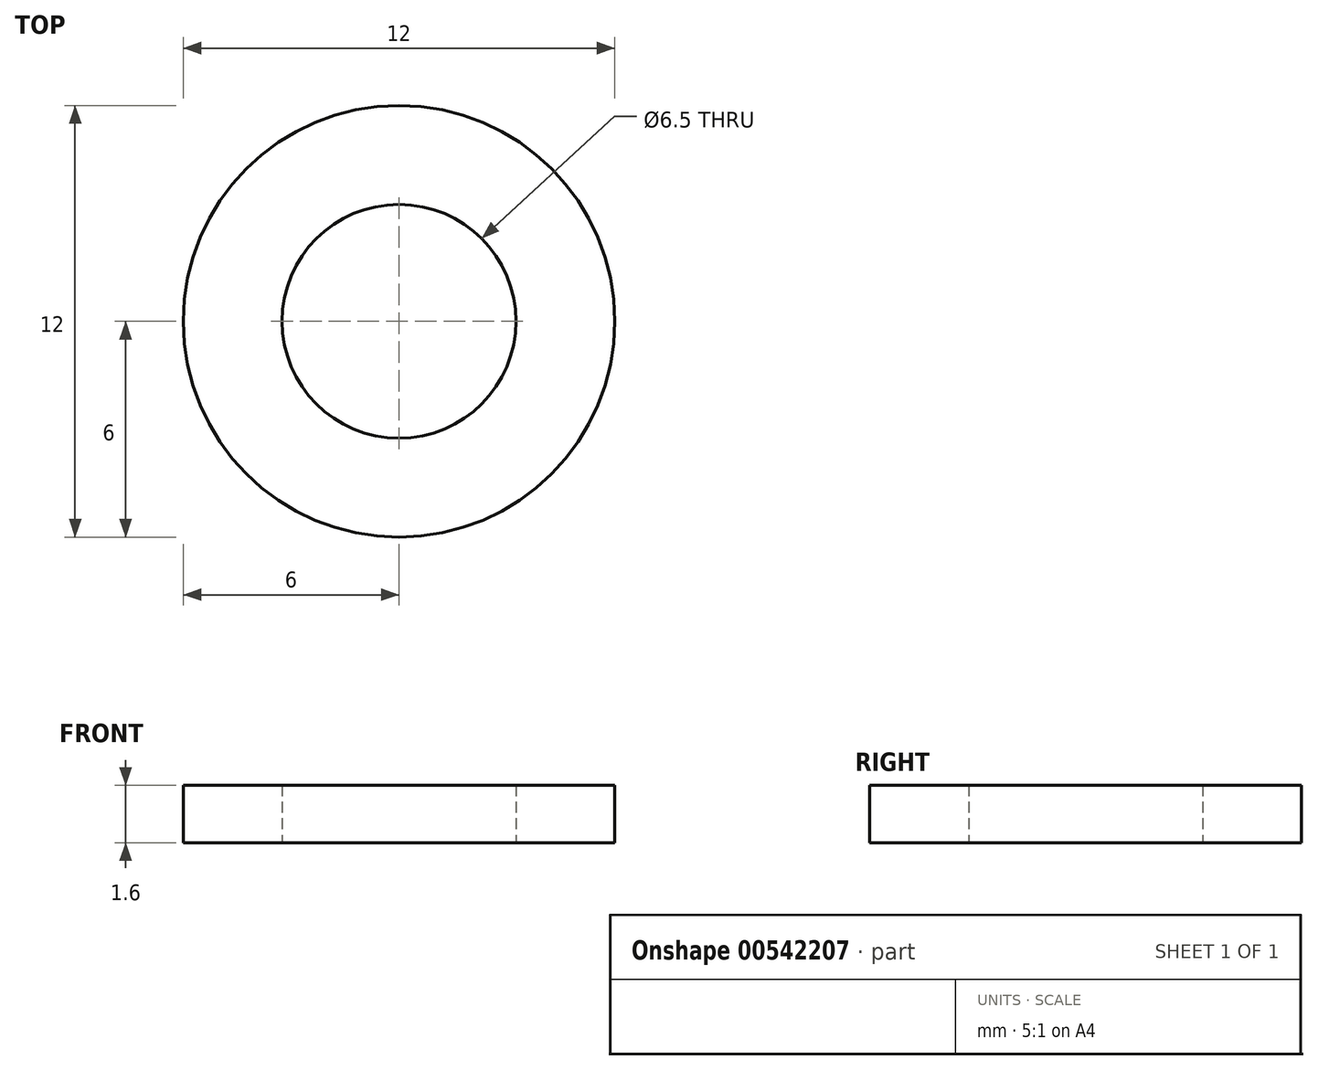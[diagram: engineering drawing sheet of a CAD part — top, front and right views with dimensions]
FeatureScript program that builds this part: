
annotation { "Feature Type Name" : "Feature", "Feature Type Description" : "" }
export const myFeature = defineFeature(function(context is Context, id is Id, definition is map)
    precondition{}
    {
        {
            var Q0;
            Q0=qCreatedBy(makeId("Top.planeOp"),FACE);
            var sketch = newSketch(context, id + "F0", { "sketchPlane" : qUnion([Q0])});
            skCircle(sketch, "E0", {"center": v(0, 0) * mm, "radius": 3.25 * mm});
            skCircle(sketch, "E1", {"center": v(0, 0) * mm, "radius": 6 * mm});
            skSolve(sketch);
        }
        {
            var Q0;
            Q0=makeQuery(id+"F0.imprint","IMPRINT",FACE,{"disambiguationData":[TD([[makeQuery(id+"F0.imprint","IMPRINT",EDGE,{"derivedFrom":sQuery(id+"F0.wireOp",EDGE,"E0")}),-1.0]])]});
            extrude(context, id + "F1", {"entities" : qUnion([Q0]), "depth" : 1.6 * mm, "offsetDistance" : 25 * mm});
        }
    });
